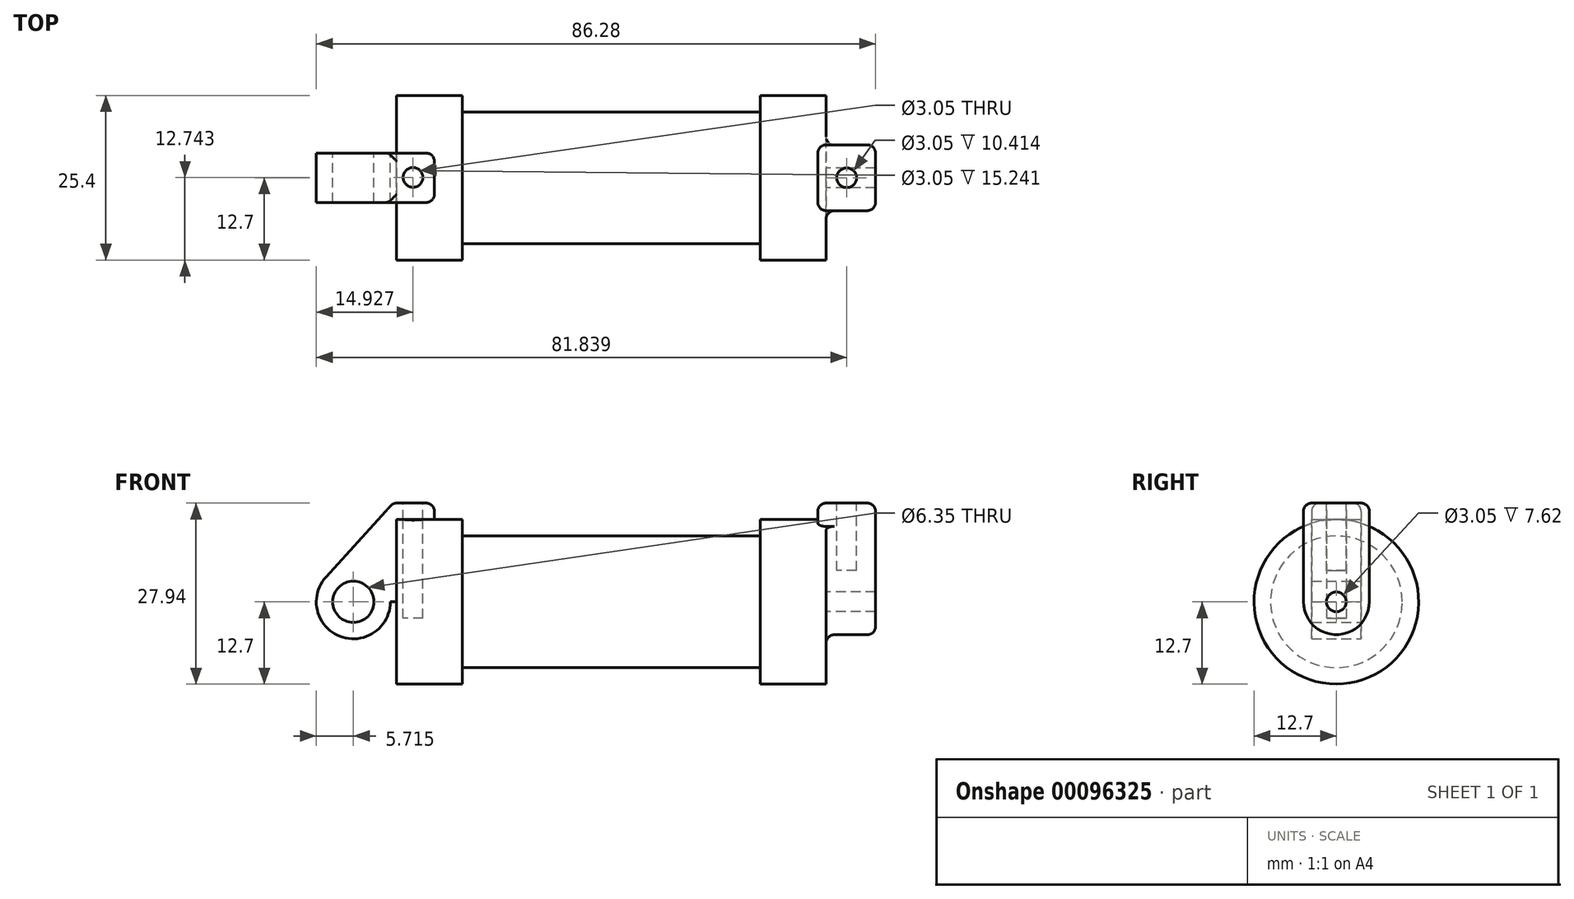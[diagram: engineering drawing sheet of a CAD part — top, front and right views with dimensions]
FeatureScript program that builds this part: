
annotation { "Feature Type Name" : "Feature", "Feature Type Description" : "" }
export const myFeature = defineFeature(function(context is Context, id is Id, definition is map)
    precondition{}
    {
        {
            var Q0;
            Q0=qCreatedBy(makeId("Front.planeOp"),FACE);
            var sketch = newSketch(context, id + "F0", { "sketchPlane" : qUnion([Q0])});
            skLineSegment(sketch, "E0", {"start": v(0, 0) * mm, "end": v(0, 12.7) * mm});
            skLineSegment(sketch, "E1", {"start": v(0, 12.7) * mm, "end": v(10.16, 12.7) * mm});
            skLineSegment(sketch, "E2", {"start": v(10.16, 12.7) * mm, "end": v(10.16, 10.16) * mm});
            skLineSegment(sketch, "E3", {"start": v(10.16, 10.16) * mm, "end": v(56.13, 10.16) * mm});
            skLineSegment(sketch, "E4", {"start": v(56.13, 10.16) * mm, "end": v(56.13, 12.7) * mm});
            skLineSegment(sketch, "E5", {"start": v(56.13, 12.7) * mm, "end": v(66.3, 12.7) * mm});
            skLineSegment(sketch, "E6", {"start": v(66.3, 12.7) * mm, "end": v(66.3, 0) * mm});
            skLineSegment(sketch, "E7", {"start": v(66.3, 0) * mm, "end": v(0, 0) * mm});
            skLineSegment(sketch, "E8", {"start": v(5.84, 15.24) * mm, "end": v(-0.5, 15.24) * mm});
            skLineSegment(sketch, "E9", {"start": v(-0.5, 15.24) * mm, "end": v(-10.88, 3.85) * mm});
            skLineSegment(sketch, "E10", {"start": v(0, 0) * mm, "end": v(-6.65, 0) * mm});
            skCircle(sketch, "E11", {"center": v(-6.65, 0) * mm, "radius": 5.72 * mm});
            skCircle(sketch, "E12", {"center": v(-6.65, 0) * mm, "radius": 3.18 * mm});
            skLineSegment(sketch, "E13", {"start": v(5.84, 15.24) * mm, "end": v(5.84, -9.4) * mm});
            skLineSegment(sketch, "E14", {"start": v(5.84, -9.4) * mm, "end": v(-8.18, -5.5) * mm});
            skText(sketch, "E15", { "text": "The Volume is : 1.622 in3", "fontName": "OpenSans-Regular.ttf"});
            const initialGuessF0  = {"E15": [-0.15467, -0.05634, 1, 0, 0.02088]};
            skSetInitialGuess(sketch, initialGuessF0);
            skSolve(sketch);
        }
        {
            var Q0;
            {var subQ0=sQuery(id+"F0.wireOp",EDGE,"E2");Q0=makeQuery(id+"F0.imprint","IMPRINT",FACE,{"disambiguationData":[TD([[makeQuery(id+"F0.imprint","IMPRINT",EDGE,{"derivedFrom":subQ0}),-1.0]])]});}
            var Q1;
            {var subQ0=sQuery(id+"F0.wireOp",EDGE,"E0");Q1=makeQuery(id+"F0.imprint","IMPRINT",FACE,{"disambiguationData":[TD([[makeQuery(id+"F0.imprint","IMPRINT",EDGE,{"derivedFrom":subQ0}),-1.0]])]});}
            var Q2;
            Q2=sQuery(id+"F0.wireOp",EDGE,"E7");
            revolve(context, id + "F1", {"entities" : qUnion([Q0, Q1]), "axis" : qUnion([Q2]), "revolveType" : RevolveType.FULL});
        }
        {
            var Q0;
            {var subQ4=sQuery(id+"F0.wireOp",EDGE,"E12");Q0=makeQuery(id+"F0.imprint","IMPRINT",FACE,{"disambiguationData":[TD([[makeQuery(id+"F0.imprint","IMPRINT",EDGE,{"derivedFrom":subQ4}),-1.0]])]});}
            var Q1;
            {var subQ3=sQuery(id+"F0.wireOp",EDGE,"E0");Q1=makeQuery(id+"F0.imprint","IMPRINT",FACE,{"disambiguationData":[TD([[makeQuery(id+"F0.imprint","IMPRINT",EDGE,{"derivedFrom":subQ3}),1.0]])]});}
            extrude(context, id + "F2", {"entities" : qUnion([Q0, Q1]), "endBound" : BoundingType.SYMMETRIC, "depth" : 7.62 * mm});
        }
        {
            var Q0;
            Q0=makeQuery(id+"F1.opRevolve","SWEPT_FACE",FACE,{"disambiguationData":[OSD([sQuery(id+"F0.wireOp",EDGE,"E6")])]});
            var sketch = newSketch(context, id + "F3", { "sketchPlane" : qUnion([Q0])});
            skCircle(sketch, "E16", {"center": v(0, 0) * mm, "radius": 5.08 * mm});
            skCircle(sketch, "E17", {"center": v(0, 0) * mm, "radius": 1.52 * mm});
            skLineSegment(sketch, "E18", {"start": v(-5.08, 0) * mm, "end": v(-5.08, 15.24) * mm});
            skLineSegment(sketch, "E19.MirrorCS", {"start": v(5.08, 0) * mm, "end": v(5.08, 15.24) * mm});
            skLineSegment(sketch, "E20", {"start": v(-5.08, 15.24) * mm, "end": v(5.08, 15.24) * mm});
            skSolve(sketch);
        }
        {
            var Q0;
            {var subQ0=sQuery(id+"F3.wireOp",EDGE,"E18");var subQ1=sQuery(id+"F3.wireOp",EDGE,"E16");var subQ2=makeQuery(id+"F3.imprint","INTERSECT",VERTEX,{"derivedFrom":[subQ1,subQ0]});Q0=makeQuery(id+"F3.imprint","IMPRINT",FACE,{"disambiguationData":[TD([[makeQuery(id+"F3.imprint","IMPRINT",EDGE,{"disambiguationData":[TD([[subQ2,1.0]])],"derivedFrom":subQ1}),-1.0]])]});}
            var Q1;
            Q1=makeQuery(id+"F3.imprint","IMPRINT",FACE,{"disambiguationData":[TD([[makeQuery(id+"F3.imprint","IMPRINT",EDGE,{"derivedFrom":sQuery(id+"F3.wireOp",EDGE,"E17")}),-1.0]])]});
            var Q2;
            {var subQ0=sQuery(id+"F3.wireOp",EDGE,"E20");Q2=makeQuery(id+"F3.imprint","IMPRINT",FACE,{"disambiguationData":[TD([[makeQuery(id+"F3.imprint","IMPRINT",EDGE,{"derivedFrom":subQ0}),-1.0]])]});}
            extrude(context, id + "F4", {"entities" : qUnion([Q0, Q1, Q2]), "operationType" : NewBodyOperationType.ADD, "depth" : 7.62 * mm});
        }
        {
            var Q0;
            Q0=makeQuery(id+"F4.opExtrude","CAP_FACE",FACE,{"disambiguationData":[OSD([sQuery(id+"F3.wireOp",EDGE,"E16"),sQuery(id+"F3.wireOp",EDGE,"E17"),sQuery(id+"F3.wireOp",EDGE,"E18"),sQuery(id+"F3.wireOp",EDGE,"E19.MirrorCS"),sQuery(id+"F3.wireOp",EDGE,"E20")])],"isStart":true});
            extrude(context, id + "F5", {"entities" : qUnion([Q0]), "operationType" : NewBodyOperationType.ADD, "depth" : 1.27 * mm});
        }
        {
            var Q0;
            Q0=makeQuery(id+"F2.opExtrude","SWEPT_FACE",FACE,{"disambiguationData":[OSD([sQuery(id+"F0.wireOp",EDGE,"E8")])]});
            var sketch = newSketch(context, id + "F6", { "sketchPlane" : qUnion([Q0])});
            skCircle(sketch, "E21", {"center": v(2.56, 0.04) * mm, "radius": 1.52 * mm});
            skLineSegment(sketch, "E22", {"start": v(-0.5, 3.81) * mm, "end": v(5.84, -3.81) * mm, "construction": true});
            skSolve(sketch);
        }
        {
            var Q0;
            {var subQ0=sQuery(id+"F3.wireOp",EDGE,"E20");Q0=makeQuery(id+"F5.boolean.opBoolean","MERGE",FACE,{"derivedFrom":[makeQuery(id+"F4.opExtrude","SWEPT_FACE",FACE,{"disambiguationData":[OSD([subQ0])]}),makeQuery(id+"F5.opExtrude","SWEPT_FACE",FACE,{"disambiguationData":[OSD([subQ0])]})]});}
            var sketch = newSketch(context, id + "F7", { "sketchPlane" : qUnion([Q0])});
            skPoint(sketch, "E23.centerSnap0", {"position": v(65.02, 0) * mm});
            skLineSegment(sketch, "E24", {"start": v(65.02, 5.08) * mm, "end": v(73.91, -5.08) * mm, "construction": true});
            skCircle(sketch, "E25", {"center": v(69.47, 0) * mm, "radius": 1.52 * mm});
            skSolve(sketch);
        }
        {
            var Q0;
            Q0 = qSketchRegion(id + "F7", true);
            extrude(context, id + "F8", {"entities" : qUnion([Q0]), "operationType" : NewBodyOperationType.REMOVE, "oppositeDirection" : true, "depth" : 10.4 * mm});
        }
        {
            var Q0;
            Q0=makeQuery(id+"F6.imprint","IMPRINT",FACE,{"disambiguationData":[TD([[makeQuery(id+"F6.imprint","IMPRINT",EDGE,{"derivedFrom":sQuery(id+"F6.wireOp",EDGE,"E21")}),1.0]])]});
            extrude(context, id + "F9", {"entities" : qUnion([Q0]), "operationType" : NewBodyOperationType.REMOVE, "oppositeDirection" : true, "depth" : 17.78 * mm});
        }
        {
            var Q0;
            {var subQ0=sQuery(id+"F3.wireOp",EDGE,"E20");var subQ1=sQuery(id+"F3.wireOp",EDGE,"E18");Q0=makeQuery(id+"F5.boolean.opBoolean","MERGE",EDGE,{"derivedFrom":[makeQuery(id+"F4.opExtrude","SWEPT_EDGE",EDGE,{"disambiguationData":[OSD([subQ1,subQ0])]}),makeQuery(id+"F5.opExtrude","SWEPT_EDGE",EDGE,{"disambiguationData":[OSD([subQ1,subQ0])]})]});}
            var Q1;
            Q1=makeQuery(id+"F4.opExtrude","CAP_EDGE",EDGE,{"disambiguationData":[OSD([sQuery(id+"F3.wireOp",EDGE,"E20")])],"isStart":false});
            var Q2;
            {var subQ0=sQuery(id+"F3.wireOp",EDGE,"E20");var subQ1=sQuery(id+"F3.wireOp",EDGE,"E19.MirrorCS");Q2=makeQuery(id+"F5.boolean.opBoolean","MERGE",EDGE,{"derivedFrom":[makeQuery(id+"F4.opExtrude","SWEPT_EDGE",EDGE,{"disambiguationData":[OSD([subQ1,subQ0])]}),makeQuery(id+"F5.opExtrude","SWEPT_EDGE",EDGE,{"disambiguationData":[OSD([subQ1,subQ0])]})]});}
            var Q3;
            Q3=makeQuery(id+"F5.opExtrude","CAP_EDGE",EDGE,{"disambiguationData":[OSD([sQuery(id+"F3.wireOp",EDGE,"E20")])],"isStart":false});
            var Q4;
            Q4=makeQuery(id+"F5.opExtrude","CAP_EDGE",EDGE,{"disambiguationData":[OSD([sQuery(id+"F3.wireOp",EDGE,"E18")])],"isStart":false});
            var Q5;
            {var subQ0=sQuery(id+"F3.wireOp",EDGE,"E18");var subQ1=sQuery(id+"F3.wireOp",EDGE,"E16");Q5=makeQuery(id+"F4.boolean.opBoolean","SPLIT",EDGE,{"disambiguationData":[TD([makeQuery(id+"F4.opExtrude","SWEPT_FACE",FACE,{"disambiguationData":[OSD([subQ1])]})])],"derivedFrom":makeQuery(id+"F4.opExtrude","CAP_EDGE",EDGE,{"disambiguationData":[OSD([subQ0])],"isStart":true})});}
            var Q6;
            Q6=makeQuery(id+"F4.opExtrude","CAP_EDGE",EDGE,{"disambiguationData":[OSD([sQuery(id+"F3.wireOp",EDGE,"E18")])],"isStart":false});
            var Q7;
            Q7=makeQuery(id+"F4.opExtrude","CAP_EDGE",EDGE,{"disambiguationData":[OSD([sQuery(id+"F3.wireOp",EDGE,"E19.MirrorCS")])],"isStart":false});
            var Q8;
            Q8=makeQuery(id+"F4.opExtrude","CAP_EDGE",EDGE,{"disambiguationData":[OSD([sQuery(id+"F3.wireOp",EDGE,"E16")])],"isStart":false});
            var Q9;
            Q9=makeQuery(id+"F4.opExtrude","CAP_EDGE",EDGE,{"disambiguationData":[OSD([sQuery(id+"F3.wireOp",EDGE,"E16")])],"isStart":true});
            var Q10;
            {var subQ0=sQuery(id+"F3.wireOp",EDGE,"E19.MirrorCS");var subQ1=sQuery(id+"F3.wireOp",EDGE,"E16");Q10=makeQuery(id+"F4.boolean.opBoolean","SPLIT",EDGE,{"disambiguationData":[TD([makeQuery(id+"F4.opExtrude","SWEPT_FACE",FACE,{"disambiguationData":[OSD([subQ1])]})])],"derivedFrom":makeQuery(id+"F4.opExtrude","CAP_EDGE",EDGE,{"disambiguationData":[OSD([subQ0])],"isStart":true})});}
            var Q11;
            Q11=makeQuery(id+"F5.opExtrude","CAP_EDGE",EDGE,{"disambiguationData":[OSD([sQuery(id+"F3.wireOp",EDGE,"E19.MirrorCS")])],"isStart":false});
            fillet(context, id + "F10", {"entities" : qUnion([Q0, Q1, Q2, Q3, Q4, Q5, Q6, Q7, Q8, Q9, Q10, Q11]), "radius" : 1.27 * mm, "tangentPropagation" : true, "allowEdgeOverflow" : false});
        }
        {
            var Q0;
            Q0=makeQuery(id+"F2.opExtrude","CAP_EDGE",EDGE,{"disambiguationData":[OSD([sQuery(id+"F0.wireOp",EDGE,"E8")])],"isStart":false});
            var Q1;
            Q1=makeQuery(id+"F2.opExtrude","SWEPT_EDGE",EDGE,{"disambiguationData":[OSD([sQuery(id+"F0.wireOp",EDGE,"E8"),sQuery(id+"F0.wireOp",EDGE,"E13")])]});
            var Q2;
            Q2=makeQuery(id+"F2.opExtrude","CAP_EDGE",EDGE,{"disambiguationData":[OSD([sQuery(id+"F0.wireOp",EDGE,"E13")])],"isStart":true});
            var Q3;
            Q3=makeQuery(id+"F2.opExtrude","SWEPT_EDGE",EDGE,{"disambiguationData":[OSD([sQuery(id+"F0.wireOp",EDGE,"E8"),sQuery(id+"F0.wireOp",EDGE,"E9")])]});
            var Q4;
            Q4=makeQuery(id+"F2.opExtrude","CAP_EDGE",EDGE,{"disambiguationData":[OSD([sQuery(id+"F0.wireOp",EDGE,"E8")])],"isStart":true});
            var Q5;
            Q5=makeQuery(id+"F2.opExtrude","CAP_EDGE",EDGE,{"disambiguationData":[OSD([sQuery(id+"F0.wireOp",EDGE,"E13")])],"isStart":false});
            fillet(context, id + "F11", {"entities" : qUnion([Q0, Q1, Q2, Q3, Q4, Q5]), "radius" : 1.27 * mm, "tangentPropagation" : true, "allowEdgeOverflow" : false});
        }
    });
